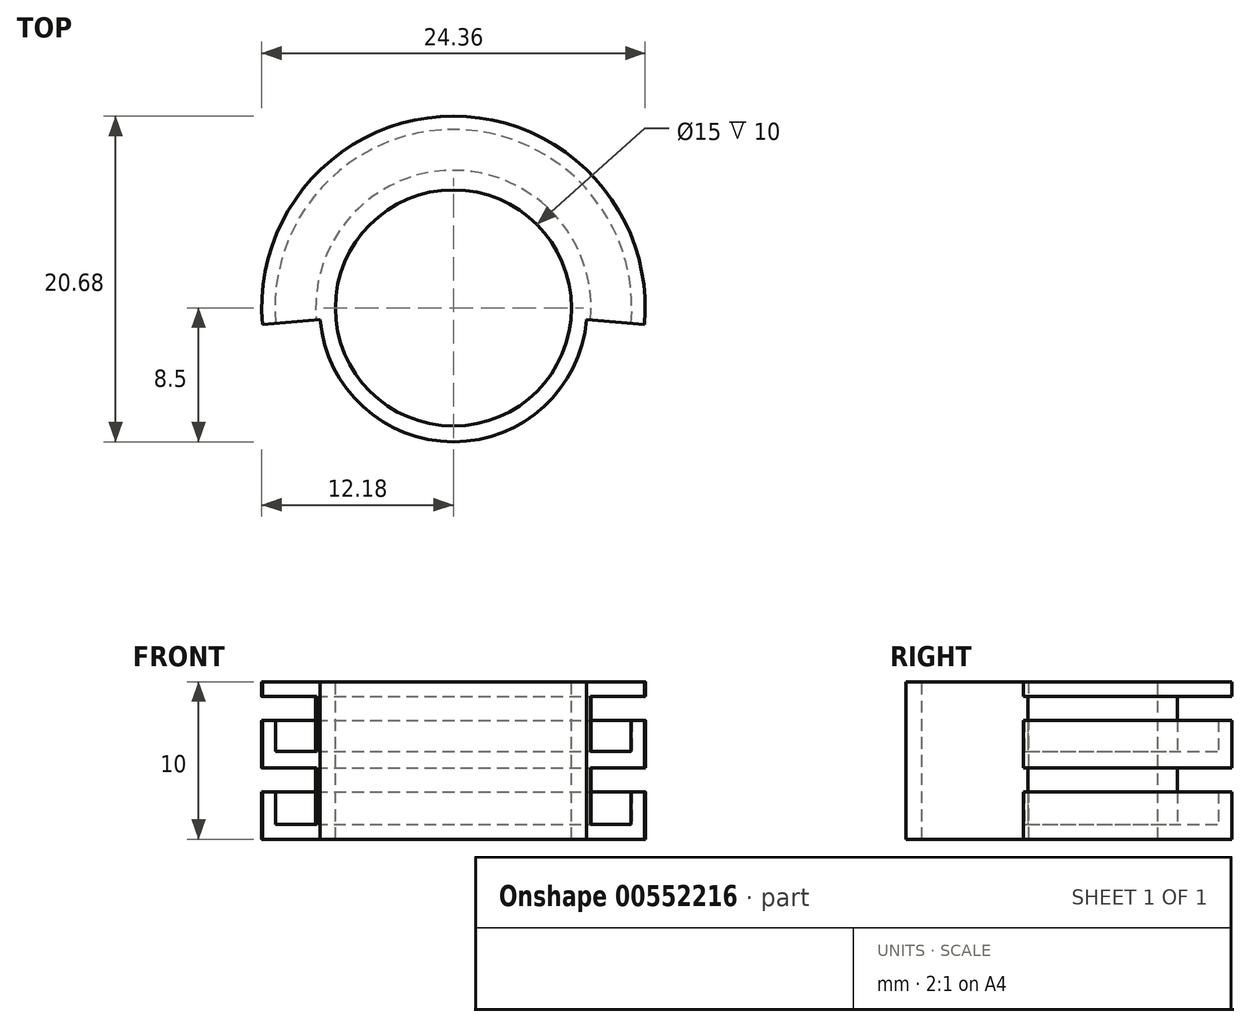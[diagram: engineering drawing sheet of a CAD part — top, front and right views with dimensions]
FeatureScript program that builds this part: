
annotation { "Feature Type Name" : "Feature", "Feature Type Description" : "" }
export const myFeature = defineFeature(function(context is Context, id is Id, definition is map)
    precondition{}
    {
        {
            var Q0;
            Q0=qCreatedBy(makeId("Top.planeOp"),FACE);
            var sketch = newSketch(context, id + "F0", { "sketchPlane" : qUnion([Q0])});
            skCircle(sketch, "E0", {"center": v(0, 0) * mm, "radius": 8.5 * mm});
            skSolve(sketch);
        }
        {
            var Q0;
            Q0=makeQuery(id+"F0.imprint","IMPRINT",FACE,{"disambiguationData":[TD([[makeQuery(id+"F0.imprint","IMPRINT",EDGE,{"derivedFrom":sQuery(id+"F0.wireOp",EDGE,"E0")}),1.0]])]});
            extrude(context, id + "F1", {"entities" : qUnion([Q0]), "endBound" : BoundingType.SYMMETRIC, "depth" : 10 * mm, "offsetDistance" : 25 * mm});
        }
        {
            var Q0;
            Q0=qCreatedBy(makeId("Top.planeOp"),FACE);
            var sketch = newSketch(context, id + "F2", { "sketchPlane" : qUnion([Q0])});
            skCircle(sketch, "E1", {"center": v(0, 0) * mm, "radius": 7.5 * mm});
            skSolve(sketch);
        }
        {
            var Q0;
            Q0 = qSketchRegion(id + "F2", true);
            extrude(context, id + "F3", {"entities" : qUnion([Q0]), "operationType" : NewBodyOperationType.REMOVE, "endBound" : BoundingType.SYMMETRIC, "oppositeDirection" : true, "depth" : 25 * mm, "offsetDistance" : 25 * mm});
        }
        {
            var Q0;
            Q0=qCreatedBy(makeId("Right.planeOp"),FACE);
            var sketch = newSketch(context, id + "F4", { "sketchPlane" : qUnion([Q0])});
            skLineSegment(sketch, "E2", {"start": v(8.27, 0) * mm, "end": v(8.27, 5) * mm});
            skLineSegment(sketch, "E3", {"start": v(8.27, 5) * mm, "end": v(12.18, 5) * mm});
            skLineSegment(sketch, "E4", {"start": v(12.18, 5) * mm, "end": v(12.18, 4.06) * mm});
            skLineSegment(sketch, "E5", {"start": v(12.18, 4.06) * mm, "end": v(8.27, 4.06) * mm});
            skLineSegment(sketch, "E6.MirrorCS", {"start": v(12.18, -4.06) * mm, "end": v(8.27, -4.06) * mm});
            skLineSegment(sketch, "E7.MirrorCS", {"start": v(12.18, -5) * mm, "end": v(12.18, -4.06) * mm});
            skLineSegment(sketch, "E8.MirrorCS", {"start": v(8.27, -5) * mm, "end": v(12.18, -5) * mm});
            skLineSegment(sketch, "E9.MirrorCS", {"start": v(8.27, 0) * mm, "end": v(8.27, -5) * mm});
            skLineSegment(sketch, "E10", {"start": v(12.18, 0) * mm, "end": v(12.18, 2.56) * mm});
            skLineSegment(sketch, "E11", {"start": v(12.18, 2.56) * mm, "end": v(11.33, 2.56) * mm});
            skLineSegment(sketch, "E12", {"start": v(11.33, 2.56) * mm, "end": v(11.33, 0.57) * mm});
            skLineSegment(sketch, "E13", {"start": v(11.33, 0.57) * mm, "end": v(8.27, 0.57) * mm});
            skLineSegment(sketch, "E14", {"start": v(12.18, -4.06) * mm, "end": v(12.18, -1.97) * mm});
            skLineSegment(sketch, "E15", {"start": v(12.18, -1.97) * mm, "end": v(11.33, -1.97) * mm});
            skLineSegment(sketch, "E16", {"start": v(11.33, -1.97) * mm, "end": v(11.33, -4.06) * mm});
            skLineSegment(sketch, "E17", {"start": v(8.27, 5) * mm, "end": v(8.74, 5) * mm});
            skLineSegment(sketch, "E18", {"start": v(8.74, 5) * mm, "end": v(8.74, -5) * mm});
            skLineSegment(sketch, "E19", {"start": v(8.74, -5) * mm, "end": v(8.27, -5) * mm});
            skLineSegment(sketch, "E20", {"start": v(12.18, 0) * mm, "end": v(12.18, -0.47) * mm});
            skLineSegment(sketch, "E21", {"start": v(12.18, -0.47) * mm, "end": v(8.27, -0.47) * mm});
            skSolve(sketch);
        }
        {
            var Q0;
            Q0 = qSketchRegion(id + "F4", true);
            var Q1;
            {var subQ2=sQuery(id+"FwEiptd1VEPaODs_1.wireOp",EDGE,"DGUKbNXq-lwat-azdn-QdOp-hOaE52hk9ped");var subQ3=sQuery(id+"F0.wireOp",EDGE,"E0");Q1=makeQuery(id+"FVkZjtNbiqLthgs_1.boolean.opBoolean","SPLIT",FACE,{"disambiguationData":[TD([makeQuery(id+"FVkZjtNbiqLthgs_1.opExtrude","SWEPT_FACE",FACE,{"disambiguationData":[OSD([subQ2])]})])],"derivedFrom":makeQuery(id+"F1.opExtrude","SWEPT_FACE",FACE,{"disambiguationData":[OSD([subQ3])]})});}
            revolve(context, id + "F5", {"operationType" : NewBodyOperationType.ADD, "entities" : qUnion([Q0]), "axis" : qUnion([Q1]), "revolveType" : RevolveType.SYMMETRIC, "oppositeDirection" : true, "angle" : 190 * degree});
        }
    });
